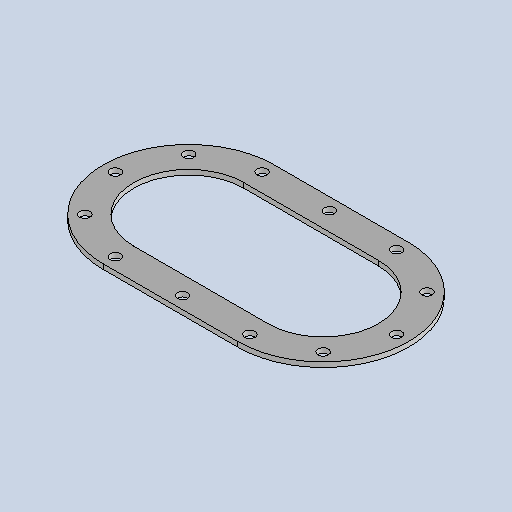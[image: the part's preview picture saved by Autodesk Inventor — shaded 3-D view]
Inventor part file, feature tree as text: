
AUTODESK INVENTOR PART (.ipt)
format: ipt  version: 2025.1 (Build 291241020, 241B)  size: 147,968 bytes
history: native  units: mm
features: sketch x3, other x3, sheet_metal_op x1, pattern_circular x1, mirror x1
ambient origin geometry x8: Origin, YZ Plane, XZ Plane, XY Plane, X Axis, Y Axis, Z Axis, Center Point
bodies: Body1 (feature_tree)
feature tree (9):
  sheet_metal_op  "Face2"
  pattern_circular  "Circular Pattern1"  Count=40  [1 undecoded]
  mirror  "Mirror1"
  sketch  "Sketch2"  dims[d12=180.0mm]
  other  "Plate2"
  sketch  "Sketch3"  dims[d13=50.0mm]
  sketch  "Sketch4"  dims[d14=8.0mm d15=17.0mm d16=20.0mm d17=8.0mm d18=0.0mm d19=50.0mm d20=180.0deg d22=0.0mm d23=8.0mm d24=0.0mm]
  other  "Cut1"
  other  "Cut2"
note: 1 required parameter value undecoded (feature->parameter linkage not recoverable at this tier; creation-order binding heuristic only, values carry confidence <= 0.55)
